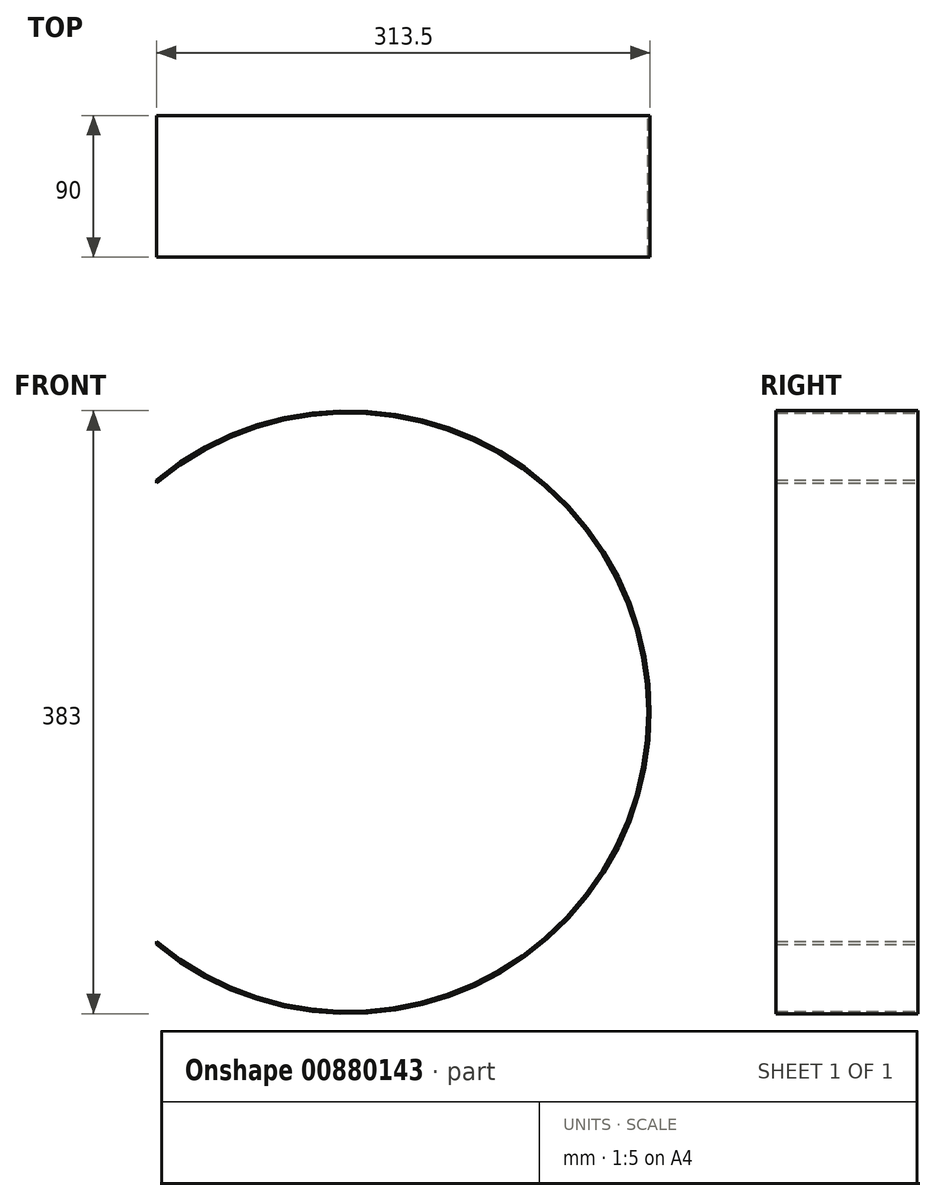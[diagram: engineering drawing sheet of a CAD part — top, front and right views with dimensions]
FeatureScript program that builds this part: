
annotation { "Feature Type Name" : "Feature", "Feature Type Description" : "" }
export const myFeature = defineFeature(function(context is Context, id is Id, definition is map)
    precondition{}
    {
        {
            var Q0;
            Q0=qCreatedBy(makeId("Front.planeOp"),FACE);
            var sketch = newSketch(context, id + "F0", { "sketchPlane" : qUnion([Q0])});
            skCircle(sketch, "E0", {"center": v(0, 0) * mm, "radius": 190 * mm});
            skCircle(sketch, "E1", {"center": v(0, 0) * mm, "radius": 191.5 * mm});
            skLineSegment(sketch, "E2", {"start": v(0, 0) * mm, "end": v(-122, 0) * mm});
            skLineSegment(sketch, "E3", {"start": v(-122, 0) * mm, "end": v(-122, 147.6) * mm});
            skLineSegment(sketch, "E4", {"start": v(-122, 147.6) * mm, "end": v(-122, -147.6) * mm});
            skSolve(sketch);
        }
        {
            var Q0;
            {var subQ0=sQuery(id+"F0.wireOp",EDGE,"E3");var subQ1=sQuery(id+"F0.wireOp",EDGE,"E0");var subQ2=makeQuery(id+"F0.imprint","INTERSECT",VERTEX,{"derivedFrom":[subQ1,subQ0]});Q0=makeQuery(id+"F0.imprint","IMPRINT",FACE,{"disambiguationData":[TD([[makeQuery(id+"F0.imprint","IMPRINT",EDGE,{"disambiguationData":[TD([[subQ2,1.0]])],"derivedFrom":subQ1}),-1.0]])]});}
            extrude(context, id + "F1", {"entities" : qUnion([Q0]), "depth" : 90 * mm, "offsetDistance" : 25 * mm});
        }
    });
